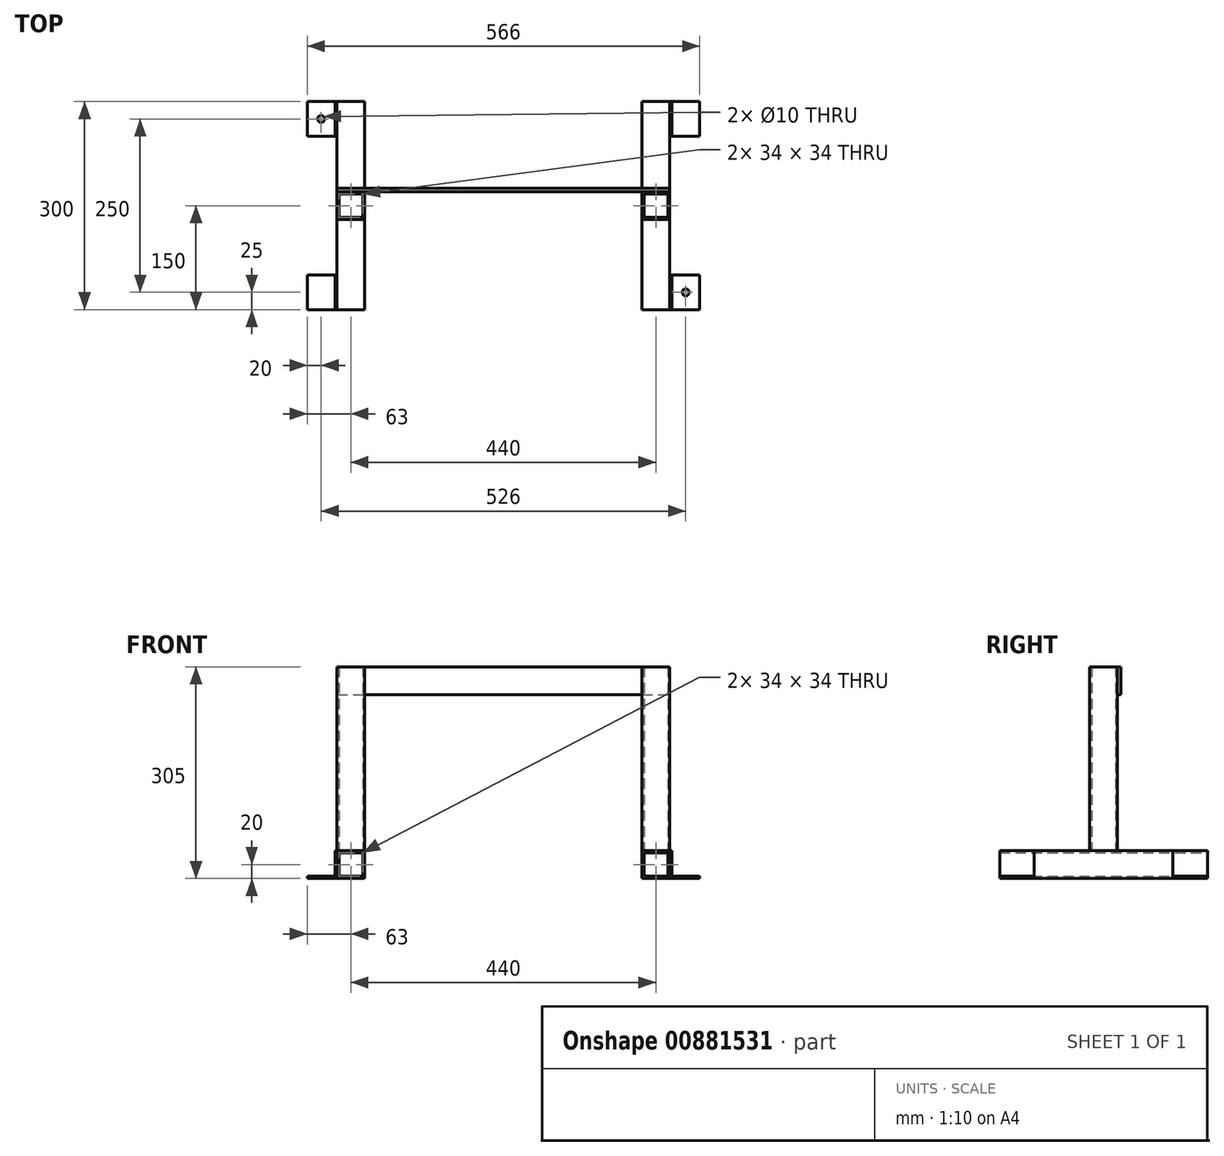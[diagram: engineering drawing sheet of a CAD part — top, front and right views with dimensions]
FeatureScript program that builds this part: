
annotation { "Feature Type Name" : "Feature", "Feature Type Description" : "" }
export const myFeature = defineFeature(function(context is Context, id is Id, definition is map)
    precondition{}
    {
        {
            var Q0;
            Q0=qCreatedBy(makeId("Front.planeOp"),FACE);
            var sketch = newSketch(context, id + "F0", { "sketchPlane" : qUnion([Q0])});
            skLineSegment(sketch, "E0", {"start": v(0, 0) * mm, "end": v(-200, 0) * mm});
            skLineSegment(sketch, "E1", {"start": v(-200, 0) * mm, "end": v(200, 0) * mm});
            skLineSegment(sketch, "E2.bottom", {"start": v(-200, 0) * mm, "end": v(-240, 0) * mm});
            skLineSegment(sketch, "E2.top", {"start": v(-200, 40) * mm, "end": v(-240, 40) * mm});
            skLineSegment(sketch, "E2.left", {"start": v(-200, 0) * mm, "end": v(-200, 40) * mm});
            skLineSegment(sketch, "E2.right", {"start": v(-240, 0) * mm, "end": v(-240, 40) * mm});
            skLineSegment(sketch, "E3", {"start": v(0, 0) * mm, "end": v(0, 28.57) * mm, "construction": true});
            skLineSegment(sketch, "E4.MirrorCS", {"start": v(200, 0) * mm, "end": v(200, 40) * mm});
            skLineSegment(sketch, "E5.MirrorCS", {"start": v(200, 40) * mm, "end": v(240, 40) * mm});
            skLineSegment(sketch, "E6.MirrorCS", {"start": v(240, 0) * mm, "end": v(240, 40) * mm});
            skLineSegment(sketch, "E7.MirrorCS", {"start": v(200, 0) * mm, "end": v(240, 0) * mm});
            skLineSegment(sketch, "E8.0", {"start": v(-237, 3) * mm, "end": v(-237, 37) * mm});
            skLineSegment(sketch, "E8.1", {"start": v(-203, 3) * mm, "end": v(-237, 3) * mm});
            skLineSegment(sketch, "E8.2", {"start": v(-203, 3) * mm, "end": v(-203, 37) * mm});
            skLineSegment(sketch, "E8.3", {"start": v(-203, 37) * mm, "end": v(-237, 37) * mm});
            skLineSegment(sketch, "E9.MirrorCS", {"start": v(203, 37) * mm, "end": v(237, 37) * mm});
            skLineSegment(sketch, "E10.MirrorCS", {"start": v(203, 3) * mm, "end": v(203, 37) * mm});
            skLineSegment(sketch, "E11.MirrorCS", {"start": v(203, 3) * mm, "end": v(237, 3) * mm});
            skLineSegment(sketch, "E12.MirrorCS", {"start": v(237, 3) * mm, "end": v(237, 37) * mm});
            skSolve(sketch);
        }
        {
            var Q0;
            Q0 = qSketchRegion(id + "F0", true);
            extrude(context, id + "F1", {"entities" : qUnion([Q0]), "depth" : 300 * mm, "offsetDistance" : 25 * mm, "symmetric" : true});
        }
        {
            var Q0;
            Q0=makeQuery(id+"F1.opExtrude","SWEPT_FACE",FACE,{"disambiguationData":[OSD([sQuery(id+"F0.wireOp",EDGE,"E2.top")])]});
            var sketch = newSketch(context, id + "F2", { "sketchPlane" : qUnion([Q0])});
            skLineSegment(sketch, "E13", {"start": v(-240, 0) * mm, "end": v(-240, 20) * mm});
            skLineSegment(sketch, "E14.bottom", {"start": v(-240, 20) * mm, "end": v(-200, 20) * mm});
            skLineSegment(sketch, "E14.top", {"start": v(-240, -20) * mm, "end": v(-200, -20) * mm});
            skLineSegment(sketch, "E14.left", {"start": v(-240, 20) * mm, "end": v(-240, -20) * mm});
            skLineSegment(sketch, "E14.right", {"start": v(-200, 20) * mm, "end": v(-200, -20) * mm});
            skLineSegment(sketch, "E15.0", {"start": v(-237, 17) * mm, "end": v(-203, 17) * mm});
            skLineSegment(sketch, "E16.0", {"start": v(-237, 17) * mm, "end": v(-237, -17) * mm});
            skLineSegment(sketch, "E17.0", {"start": v(-237, -17) * mm, "end": v(-203, -17) * mm});
            skLineSegment(sketch, "E18.0", {"start": v(-203, 17) * mm, "end": v(-203, -17) * mm});
            skLineSegment(sketch, "E19", {"start": v(0, 0) * mm, "end": v(0, 43.2) * mm, "construction": true});
            skLineSegment(sketch, "E20.MirrorCS", {"start": v(200, 20) * mm, "end": v(200, -20) * mm});
            skLineSegment(sketch, "E21.MirrorCS", {"start": v(240, 20) * mm, "end": v(200, 20) * mm});
            skLineSegment(sketch, "E22.MirrorCS", {"start": v(240, 20) * mm, "end": v(240, -20) * mm});
            skLineSegment(sketch, "E23.MirrorCS", {"start": v(240, -20) * mm, "end": v(200, -20) * mm});
            skLineSegment(sketch, "E24.MirrorCS", {"start": v(237, -17) * mm, "end": v(203, -17) * mm});
            skLineSegment(sketch, "E25.MirrorCS", {"start": v(237, 17) * mm, "end": v(237, -17) * mm});
            skLineSegment(sketch, "E26.MirrorCS", {"start": v(237, 17) * mm, "end": v(203, 17) * mm});
            skLineSegment(sketch, "E27.MirrorCS", {"start": v(203, 17) * mm, "end": v(203, -17) * mm});
            skSolve(sketch);
        }
        {
            var Q0;
            Q0 = qSketchRegion(id + "F2", true);
            extrude(context, id + "F3", {"entities" : qUnion([Q0]), "depth" : 265 * mm, "offsetDistance" : 25 * mm});
        }
        {
            var Q0;
            Q0=makeQuery(id+"F1.opExtrude","CAP_FACE",FACE,{"disambiguationData":[OSD([sQuery(id+"F0.wireOp",EDGE,"E2.bottom"),sQuery(id+"F0.wireOp",EDGE,"E2.top"),sQuery(id+"F0.wireOp",EDGE,"E2.left"),sQuery(id+"F0.wireOp",EDGE,"E2.right"),sQuery(id+"F0.wireOp",EDGE,"E8.0"),sQuery(id+"F0.wireOp",EDGE,"E8.1"),sQuery(id+"F0.wireOp",EDGE,"E8.2"),sQuery(id+"F0.wireOp",EDGE,"E8.3")])],"isStart":false});
            var sketch = newSketch(context, id + "F4", { "sketchPlane" : qUnion([Q0])});
            skLineSegment(sketch, "E28", {"start": v(-240, 40) * mm, "end": v(-243, 40) * mm});
            skLineSegment(sketch, "E29", {"start": v(-243, 40) * mm, "end": v(-243, 3) * mm});
            skLineSegment(sketch, "E30", {"start": v(-243, 3) * mm, "end": v(-283, 3) * mm});
            skLineSegment(sketch, "E31", {"start": v(-283, 3) * mm, "end": v(-283, 0) * mm});
            skLineSegment(sketch, "E32", {"start": v(-283, 0) * mm, "end": v(-240, 0) * mm});
            skLineSegment(sketch, "E33.MirrorCS", {"start": v(243, 3) * mm, "end": v(283, 3) * mm});
            skLineSegment(sketch, "E34.MirrorCS", {"start": v(283, 0) * mm, "end": v(240, 0) * mm});
            skLineSegment(sketch, "E35.MirrorCS", {"start": v(243, 40) * mm, "end": v(243, 3) * mm});
            skLineSegment(sketch, "E36.MirrorCS", {"start": v(240, 40) * mm, "end": v(243, 40) * mm});
            skLineSegment(sketch, "E37.MirrorCS", {"start": v(283, 3) * mm, "end": v(283, 0) * mm});
            skLineSegment(sketch, "E38", {"start": v(-240, 40) * mm, "end": v(-240, 0) * mm});
            skLineSegment(sketch, "E39.MirrorCS", {"start": v(240, 40) * mm, "end": v(240, 0) * mm});
            skSolve(sketch);
        }
        {
            var Q0;
            Q0=makeQuery(id+"F4.imprint","IMPRINT",FACE,{"disambiguationData":[TD([[makeQuery(id+"F4.imprint","IMPRINT",EDGE,{"derivedFrom":sQuery(id+"F4.wireOp",EDGE,"E28")}),1.0]])]});
            var Q1;
            Q1=makeQuery(id+"F4.imprint","IMPRINT",FACE,{"disambiguationData":[TD([[makeQuery(id+"F4.imprint","IMPRINT",EDGE,{"derivedFrom":sQuery(id+"F4.wireOp",EDGE,"E33.MirrorCS")}),-1.0]])]});
            extrude(context, id + "F5", {"entities" : qUnion([Q0, Q1]), "oppositeDirection" : true, "depth" : 50 * mm, "offsetDistance" : 25 * mm});
        }
        {
            var Q0;
            Q0=makeQuery(id+"F5.opExtrude","SWEPT_BODY",BODY,{"disambiguationData":[OSD([sQuery(id+"F4.wireOp",EDGE,"E33.MirrorCS"),sQuery(id+"F4.wireOp",EDGE,"E34.MirrorCS"),sQuery(id+"F4.wireOp",EDGE,"E35.MirrorCS"),sQuery(id+"F4.wireOp",EDGE,"E36.MirrorCS"),sQuery(id+"F4.wireOp",EDGE,"E37.MirrorCS"),sQuery(id+"F4.wireOp",EDGE,"E39.MirrorCS")])]});
            var Q1;
            Q1=qCreatedBy(makeId("Front.planeOp"),FACE);
            mirror(context, id + "F6", {"entities" : qUnion([Q0]), "mirrorPlane" : qUnion([Q1])});
        }
        {
            var Q0;
            Q0=makeQuery(id+"F1.opExtrude","CAP_FACE",FACE,{"disambiguationData":[OSD([sQuery(id+"F0.wireOp",EDGE,"E2.bottom"),sQuery(id+"F0.wireOp",EDGE,"E2.top"),sQuery(id+"F0.wireOp",EDGE,"E2.left"),sQuery(id+"F0.wireOp",EDGE,"E2.right"),sQuery(id+"F0.wireOp",EDGE,"E8.0"),sQuery(id+"F0.wireOp",EDGE,"E8.1"),sQuery(id+"F0.wireOp",EDGE,"E8.2"),sQuery(id+"F0.wireOp",EDGE,"E8.3")])],"isStart":true});
            var sketch = newSketch(context, id + "F7", { "sketchPlane" : qUnion([Q0])});
            skLineSegment(sketch, "E40.0.0", {"start": v(283, 0) * mm, "end": v(283, 3) * mm});
            skLineSegment(sketch, "E40.0.1", {"start": v(283, 3) * mm, "end": v(243, 3) * mm});
            skLineSegment(sketch, "E40.0.2", {"start": v(243, 3) * mm, "end": v(243, 40) * mm});
            skLineSegment(sketch, "E40.0.3", {"start": v(243, 40) * mm, "end": v(240, 40) * mm});
            skLineSegment(sketch, "E40.0.4", {"start": v(240, 40) * mm, "end": v(240, 0) * mm});
            skLineSegment(sketch, "E40.0.5", {"start": v(240, 0) * mm, "end": v(283, 0) * mm});
            skSolve(sketch);
        }
        {
            var Q0;
            Q0=makeQuery(id+"F7.imprint","IMPRINT",FACE,{"disambiguationData":[TD([[makeQuery(id+"F7.imprint","IMPRINT",EDGE,{"derivedFrom":sQuery(id+"F7.wireOp",EDGE,"E40.0.0")}),1.0]])]});
            extrude(context, id + "F8", {"entities" : qUnion([Q0]), "oppositeDirection" : true, "depth" : 50 * mm, "offsetDistance" : 25 * mm});
        }
        {
            var Q0;
            Q0=makeQuery(id+"F3.opExtrude","SWEPT_FACE",FACE,{"disambiguationData":[OSD([sQuery(id+"F2.wireOp",EDGE,"E14.bottom")])]});
            var sketch = newSketch(context, id + "F9", { "sketchPlane" : qUnion([Q0])});
            skLineSegment(sketch, "E41.bottom", {"start": v(240, 305) * mm, "end": v(-240, 305) * mm});
            skLineSegment(sketch, "E41.top", {"start": v(240, 265) * mm, "end": v(-240, 265) * mm});
            skLineSegment(sketch, "E41.left", {"start": v(240, 305) * mm, "end": v(240, 265) * mm});
            skLineSegment(sketch, "E41.right", {"start": v(-240, 305) * mm, "end": v(-240, 265) * mm});
            skSolve(sketch);
        }
        {
            var Q0;
            {var subQ3=sQuery(id+"F9.wireOp",EDGE,"E41.right");Q0=makeQuery(id+"F9.imprint","IMPRINT",FACE,{"disambiguationData":[TD([[makeQuery(id+"F9.imprint","IMPRINT",EDGE,{"derivedFrom":subQ3}),1.0]])]});}
            var Q1;
            {var subQ0=sQuery(id+"F9.wireOp",EDGE,"E41.left");Q1=makeQuery(id+"F9.imprint","IMPRINT",FACE,{"disambiguationData":[TD([[makeQuery(id+"F9.imprint","IMPRINT",EDGE,{"derivedFrom":subQ0}),-1.0]])]});}
            extrude(context, id + "F10", {"entities" : qUnion([Q0, Q1]), "depth" : 5 * mm, "offsetDistance" : 25 * mm});
        }
        {
            var Q0;
            Q0=makeQuery(id+"F8.opExtrude","SWEPT_FACE",FACE,{"disambiguationData":[OSD([sQuery(id+"F7.wireOp",EDGE,"E40.0.1")])]});
            var sketch = newSketch(context, id + "F11", { "sketchPlane" : qUnion([Q0])});
            skLineSegment(sketch, "E42.0.0", {"start": v(-243, 150) * mm, "end": v(-283, 150) * mm});
            skLineSegment(sketch, "E42.0.1", {"start": v(-283, 150) * mm, "end": v(-283, 100) * mm});
            skLineSegment(sketch, "E42.0.2", {"start": v(-283, 100) * mm, "end": v(-243, 100) * mm});
            skLineSegment(sketch, "E42.0.3", {"start": v(-243, 100) * mm, "end": v(-243, 150) * mm});
            skLineSegment(sketch, "E43", {"start": v(-263, 150) * mm, "end": v(-263, 100) * mm});
            skCircle(sketch, "E44", {"center": v(-263, 125) * mm, "radius": 5 * mm});
            skLineSegment(sketch, "E45", {"start": v(-263, 125) * mm, "end": v(-283, 125) * mm});
            skLineSegment(sketch, "E46", {"start": v(0, 0) * mm, "end": v(0, 58.97) * mm, "construction": true});
            skLineSegment(sketch, "E47", {"start": v(0, 0) * mm, "end": v(-42.42, 0) * mm, "construction": true});
            skCircle(sketch, "E48.MirrorC", {"center": v(263, 125) * mm, "radius": 5 * mm});
            skCircle(sketch, "E49.MirrorC", {"center": v(-263, -125) * mm, "radius": 5 * mm});
            skCircle(sketch, "E50.MirrorC", {"center": v(263, -125) * mm, "radius": 5 * mm});
            skSolve(sketch);
        }
        {
            var Q0;
            {var subQ0=sQuery(id+"F11.wireOp",EDGE,"E43");var subQ1=makeQuery(id+"F11.imprint","INTERSECT",VERTEX,{"derivedFrom":[subQ0,sQuery(id+"F11.wireOp",EDGE,"E45")]});Q0=makeQuery(id+"F11.imprint","IMPRINT",FACE,{"disambiguationData":[TD([[makeQuery(id+"F11.imprint","IMPRINT",EDGE,{"disambiguationData":[TD([[subQ1,1.0]])],"derivedFrom":subQ0}),1.0]])]});}
            var Q1;
            {var subQ0=sQuery(id+"F11.wireOp",EDGE,"E45");var subQ1=sQuery(id+"F11.wireOp",EDGE,"E43");var subQ2=makeQuery(id+"F11.imprint","INTERSECT",VERTEX,{"derivedFrom":[subQ1,subQ0]});Q1=makeQuery(id+"F11.imprint","IMPRINT",FACE,{"disambiguationData":[TD([[makeQuery(id+"F11.imprint","IMPRINT",EDGE,{"disambiguationData":[TD([[subQ2,-1.0]])],"derivedFrom":subQ1}),-1.0]])]});}
            var Q2;
            {var subQ0=sQuery(id+"F11.wireOp",EDGE,"E45");var subQ1=sQuery(id+"F11.wireOp",EDGE,"E43");var subQ2=makeQuery(id+"F11.imprint","INTERSECT",VERTEX,{"derivedFrom":[subQ1,subQ0]});Q2=makeQuery(id+"F11.imprint","IMPRINT",FACE,{"disambiguationData":[TD([[makeQuery(id+"F11.imprint","IMPRINT",EDGE,{"disambiguationData":[TD([[subQ2,1.0]])],"derivedFrom":subQ1}),-1.0]])]});}
            var Q3;
            Q3=makeQuery(id+"F11.imprint","IMPRINT",FACE,{"disambiguationData":[TD([[makeQuery(id+"F11.imprint","IMPRINT",EDGE,{"derivedFrom":sQuery(id+"F11.wireOp",EDGE,"E49.MirrorC")}),-1.0]])]});
            var Q4;
            Q4=makeQuery(id+"F11.imprint","IMPRINT",FACE,{"disambiguationData":[TD([[makeQuery(id+"F11.imprint","IMPRINT",EDGE,{"derivedFrom":sQuery(id+"F11.wireOp",EDGE,"E50.MirrorC")}),1.0]])]});
            var Q5;
            Q5=makeQuery(id+"F11.imprint","IMPRINT",FACE,{"disambiguationData":[TD([[makeQuery(id+"F11.imprint","IMPRINT",EDGE,{"derivedFrom":sQuery(id+"F11.wireOp",EDGE,"E48.MirrorC")}),-1.0]])]});
            extrude(context, id + "F12", {"entities" : qUnion([Q0, Q1, Q2, Q3, Q4, Q5]), "operationType" : NewBodyOperationType.REMOVE, "oppositeDirection" : true, "depth" : 25 * mm, "offsetDistance" : 25 * mm});
        }
    });
